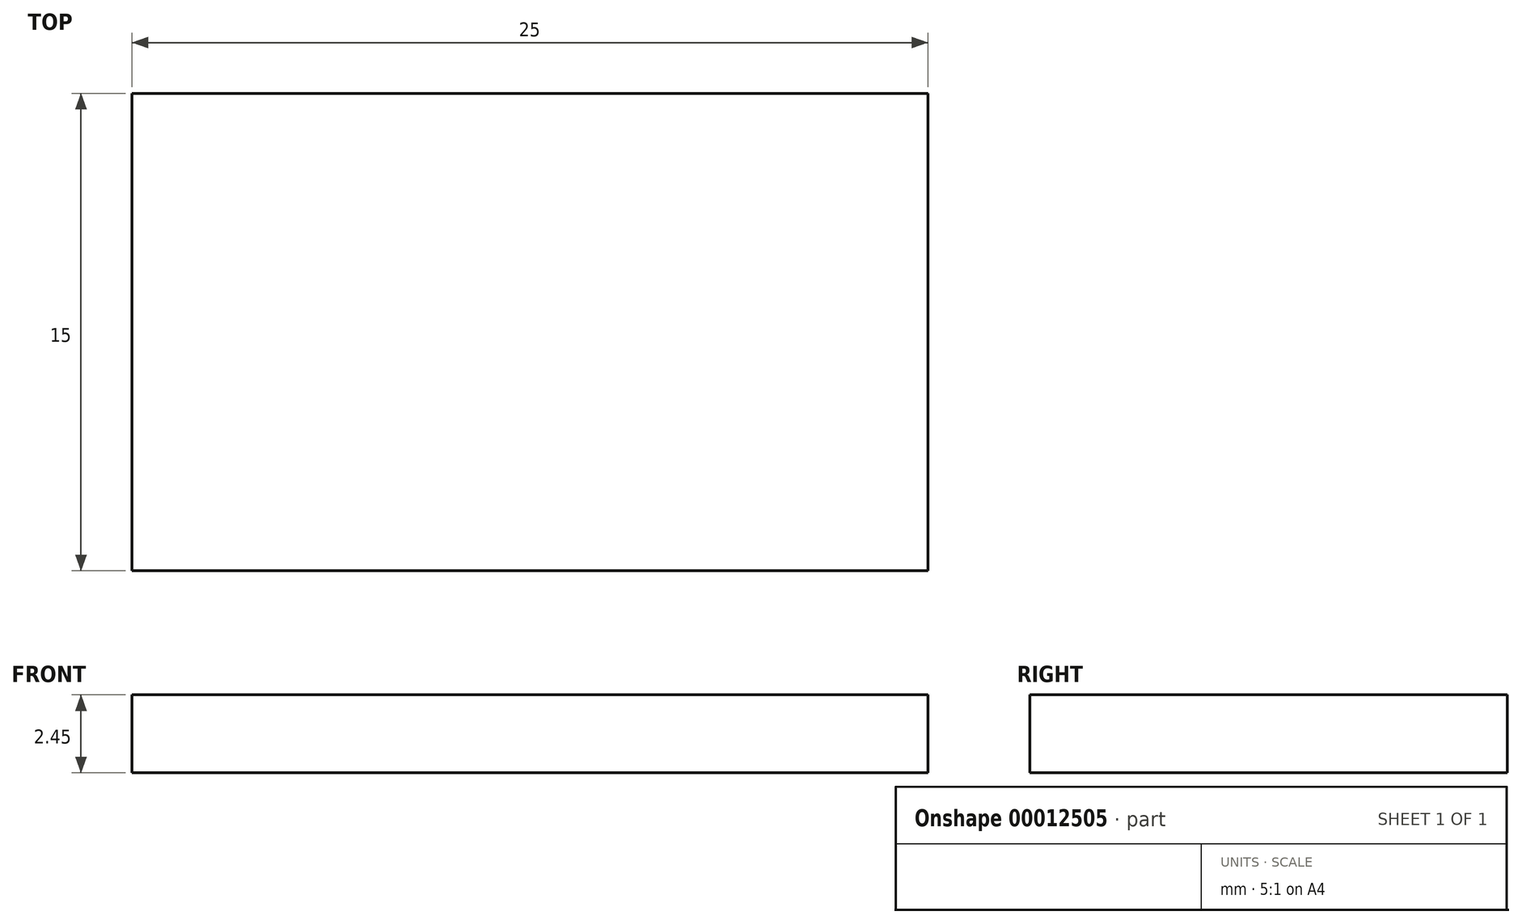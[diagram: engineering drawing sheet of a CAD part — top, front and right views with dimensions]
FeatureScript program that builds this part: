
annotation { "Feature Type Name" : "Feature", "Feature Type Description" : "" }
export const myFeature = defineFeature(function(context is Context, id is Id, definition is map)
    precondition{}
    {
        {
            var Q0;
            Q0=qCreatedBy(makeId("Top.planeOp"),FACE);
            var sketch = newSketch(context, id + "F0", { "sketchPlane" : qUnion([Q0])});
            skLineSegment(sketch, "E0.rect.bottom", {"start": v(12.5, -7.5) * mm, "end": v(-12.5, -7.5) * mm});
            skLineSegment(sketch, "E0.rect.top", {"start": v(12.5, 7.5) * mm, "end": v(-12.5, 7.5) * mm});
            skLineSegment(sketch, "E0.rect.left", {"start": v(12.5, -7.5) * mm, "end": v(12.5, 7.5) * mm});
            skLineSegment(sketch, "E0.rect.right", {"start": v(-12.5, -7.5) * mm, "end": v(-12.5, 7.5) * mm});
            skPoint(sketch, "E0.rect.middle", {"position": v(0, 0) * mm});
            skSolve(sketch);
        }
        {
            var Q0;
            Q0=makeQuery(id+"F0.imprint","IMPRINT",FACE,{"disambiguationData":[TD([[makeQuery(id+"F0.imprint","IMPRINT",EDGE,{"derivedFrom":sQuery(id+"F0.wireOp",EDGE,"E0.rect.bottom")}),-1.0]])]});
            extrude(context, id + "F1", {"entities" : qUnion([Q0]), "depth" : 2.45 * mm});
        }
    });
